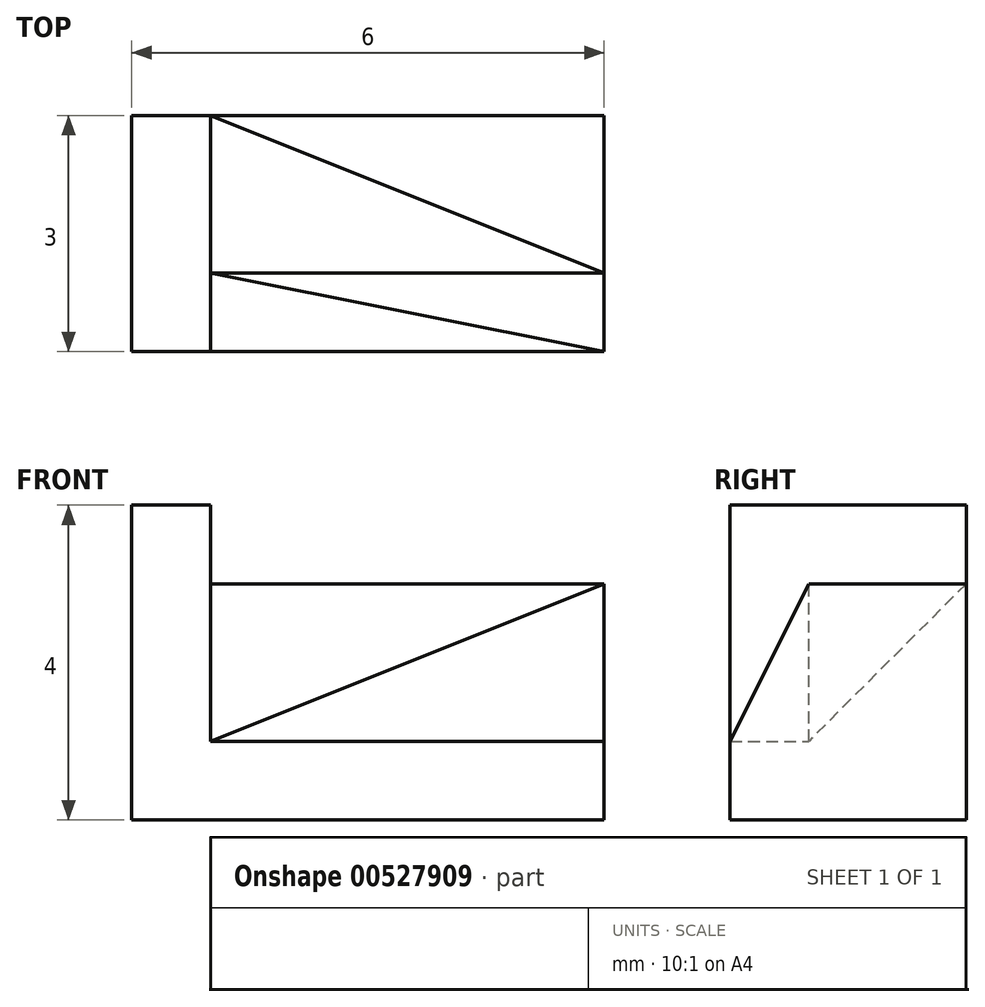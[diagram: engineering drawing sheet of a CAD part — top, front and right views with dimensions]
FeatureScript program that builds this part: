
annotation { "Feature Type Name" : "Feature", "Feature Type Description" : "" }
export const myFeature = defineFeature(function(context is Context, id is Id, definition is map)
    precondition{}
    {
        {
            var Q0;
            Q0=qCreatedBy(makeId("Top.planeOp"),FACE);
            var sketch = newSketch(context, id + "F0", { "sketchPlane" : qUnion([Q0])});
            skLineSegment(sketch, "E0.bottom", {"start": v(0, 0) * mm, "end": v(5, 0) * mm});
            skLineSegment(sketch, "E0.top", {"start": v(0, 3) * mm, "end": v(5, 3) * mm});
            skLineSegment(sketch, "E0.left", {"start": v(0, 0) * mm, "end": v(0, 3) * mm});
            skLineSegment(sketch, "E0.right", {"start": v(5, 0) * mm, "end": v(5, 3) * mm});
            skSolve(sketch);
        }
        {
            var Q0;
            Q0=qSketchRegion(id+"F0",true);
            extrude(context, id + "F1", {"entities" : qUnion([Q0]), "depth" : 3 * mm});
        }
        {
            var Q0;
            Q0=makeQuery(id+"F1.opExtrude","CAP_FACE",FACE,{"disambiguationData":[OSD([sQuery(id+"F0.wireOp",EDGE,"E0.bottom"),sQuery(id+"F0.wireOp",EDGE,"E0.top"),sQuery(id+"F0.wireOp",EDGE,"E0.left"),sQuery(id+"F0.wireOp",EDGE,"E0.right")])],"isStart":false});
            var sketch = newSketch(context, id + "F2", { "sketchPlane" : qUnion([Q0])});
            skLineSegment(sketch, "E1", {"start": v(0, 0) * mm, "end": v(5, 0) * mm});
            skLineSegment(sketch, "E2", {"start": v(5, 0) * mm, "end": v(0, 1) * mm});
            skLineSegment(sketch, "E3", {"start": v(0, 1) * mm, "end": v(0, 0) * mm});
            skSolve(sketch);
        }
        {
            var Q0;
            Q0=qSketchRegion(id+"F2",true);
            extrude(context, id + "F3", {"entities" : qUnion([Q0]), "operationType" : NewBodyOperationType.REMOVE, "oppositeDirection" : true, "depth" : 2 * mm});
        }
        {
            var Q0;
            Q0=makeQuery(id+"F1.opExtrude","SWEPT_FACE",FACE,{"disambiguationData":[OSD([sQuery(id+"F0.wireOp",EDGE,"E0.right")])]});
            var sketch = newSketch(context, id + "F4", { "sketchPlane" : qUnion([Q0])});
            skLineSegment(sketch, "E4", {"start": v(0, 0) * mm, "end": v(1, 0) * mm, "construction": true});
            skLineSegment(sketch, "E5", {"start": v(1, 0) * mm, "end": v(1, 3) * mm, "construction": true});
            skSolve(sketch);
        }
        {
            var Q0;
            Q0=makeQuery(id+"F3.boolean.opBoolean","COPY",VERTEX,{"derivedFrom":makeQuery(id+"F3.opExtrude","CAP_VERTEX",VERTEX,{"disambiguationData":[OSD([sQuery(id+"F0.wireOp",EDGE,"E0.left"),sQuery(id+"F2.wireOp",EDGE,"E2"),sQuery(id+"F2.wireOp",EDGE,"E3")])],"isStart":false})});
            var Q1;
            Q1=makeQuery(id+"F3.boolean.opBoolean","COPY",VERTEX,{"derivedFrom":makeQuery(id+"F3.opExtrude","CAP_VERTEX",VERTEX,{"disambiguationData":[OSD([sQuery(id+"F0.wireOp",EDGE,"E0.right"),sQuery(id+"F2.wireOp",EDGE,"E1"),sQuery(id+"F2.wireOp",EDGE,"E2")])],"isStart":false})});
            var Q2;
            Q2=sQuery(id+"F4.wireOp",VERTEX,"E5.end");
            cPlane(context, id + "F5", {"entities" : qUnion([Q0, Q1, Q2]), "cplaneType" : CPlaneType.THREE_POINT, "offset" : 25 * mm, "width" : 150 * mm, "height" : 150 * mm});
        }
        {
            var Q0;
            Q0=qCreatedBy(id+"F5.planeOp",FACE);
            var sketch = newSketch(context, id + "F6", { "sketchPlane" : qUnion([Q0])});
            skPoint(sketch, "E6.0", {"position": v(0.08, 1.34) * mm});
            skPoint(sketch, "E6.1", {"position": v(-5, 3.13) * mm});
            skPoint(sketch, "E6.2", {"position": v(-5, 0.9) * mm});
            skLineSegment(sketch, "E7", {"start": v(0.08, 1.34) * mm, "end": v(-5, 3.13) * mm});
            skLineSegment(sketch, "E8", {"start": v(0.08, 1.34) * mm, "end": v(-5, 0.9) * mm});
            skLineSegment(sketch, "E9", {"start": v(-5, 3.13) * mm, "end": v(-5.73, 3.13) * mm});
            skLineSegment(sketch, "E10", {"start": v(-5, 0.9) * mm, "end": v(-5.73, 0.9) * mm});
            skLineSegment(sketch, "E11", {"start": v(-5.73, 0.9) * mm, "end": v(-5.73, 3.13) * mm});
            skSolve(sketch);
        }
        {
            var Q0;
            Q0=qSketchRegion(id+"F6",true);
            extrude(context, id + "F7", {"entities" : qUnion([Q0]), "operationType" : NewBodyOperationType.REMOVE, "oppositeDirection" : true, "depth" : 25 * mm});
        }
        {
            var Q0;
            Q0=makeQuery(id+"F7.boolean.opBoolean","MERGE",VERTEX,{"derivedFrom":[makeQuery(id+"F3.boolean.opBoolean","COPY",VERTEX,{"derivedFrom":makeQuery(id+"F3.opExtrude","CAP_VERTEX",VERTEX,{"disambiguationData":[OSD([sQuery(id+"F0.wireOp",EDGE,"E0.left"),sQuery(id+"F2.wireOp",EDGE,"E2"),sQuery(id+"F2.wireOp",EDGE,"E3")])],"isStart":false})}),makeQuery(id+"F7.opExtrude","CAP_VERTEX",VERTEX,{"disambiguationData":[OSD([sQuery(id+"F6.wireOp",EDGE,"E7"),sQuery(id+"F6.wireOp",EDGE,"E8")])],"isStart":true})]});
            var Q1;
            Q1=sQuery(id+"F4.wireOp",VERTEX,"E5.end");
            var Q2;
            Q2=makeQuery(id+"F1.opExtrude","CAP_VERTEX",VERTEX,{"disambiguationData":[OSD([sQuery(id+"F0.wireOp",EDGE,"E0.top"),sQuery(id+"F0.wireOp",EDGE,"E0.left")])],"isStart":false});
            cPlane(context, id + "F8", {"entities" : qUnion([Q0, Q1, Q2]), "cplaneType" : CPlaneType.THREE_POINT, "offset" : 25 * mm, "width" : 150 * mm, "height" : 150 * mm});
        }
        {
            var Q0;
            Q0=qCreatedBy(id+"F8.planeOp",FACE);
            var sketch = newSketch(context, id + "F9", { "sketchPlane" : qUnion([Q0])});
            skPoint(sketch, "E12.0", {"position": v(0, 1.41) * mm});
            skPoint(sketch, "E12.1", {"position": v(0, 4.24) * mm});
            skPoint(sketch, "E12.2", {"position": v(-5.2, 2.83) * mm});
            skLineSegment(sketch, "E13", {"start": v(-5.2, 2.83) * mm, "end": v(0, 4.24) * mm});
            skLineSegment(sketch, "E14", {"start": v(0, 4.24) * mm, "end": v(0, 1.41) * mm});
            skLineSegment(sketch, "E15", {"start": v(-5.2, 2.83) * mm, "end": v(-5.48, 1.8) * mm});
            skLineSegment(sketch, "E16", {"start": v(-5.48, 1.8) * mm, "end": v(0, 1.41) * mm});
            skSolve(sketch);
        }
        {
            var Q0;
            Q0=qSketchRegion(id+"F9",true);
            extrude(context, id + "F10", {"entities" : qUnion([Q0]), "operationType" : NewBodyOperationType.REMOVE, "oppositeDirection" : true, "depth" : 25 * mm});
        }
        {
            var Q0;
            Q0=qCreatedBy(makeId("Top.planeOp"),FACE);
            var sketch = newSketch(context, id + "F11", { "sketchPlane" : qUnion([Q0])});
            skLineSegment(sketch, "E17.bottom", {"start": v(0, 0) * mm, "end": v(-1, 0) * mm});
            skLineSegment(sketch, "E17.top", {"start": v(0, 3) * mm, "end": v(-1, 3) * mm});
            skLineSegment(sketch, "E17.left", {"start": v(0, 0) * mm, "end": v(0, 3) * mm});
            skLineSegment(sketch, "E17.right", {"start": v(-1, 0) * mm, "end": v(-1, 3) * mm});
            skSolve(sketch);
        }
        {
            var Q0;
            Q0=qSketchRegion(id+"F11",true);
            extrude(context, id + "F12", {"entities" : qUnion([Q0]), "operationType" : NewBodyOperationType.ADD, "depth" : 4 * mm});
        }
    });
